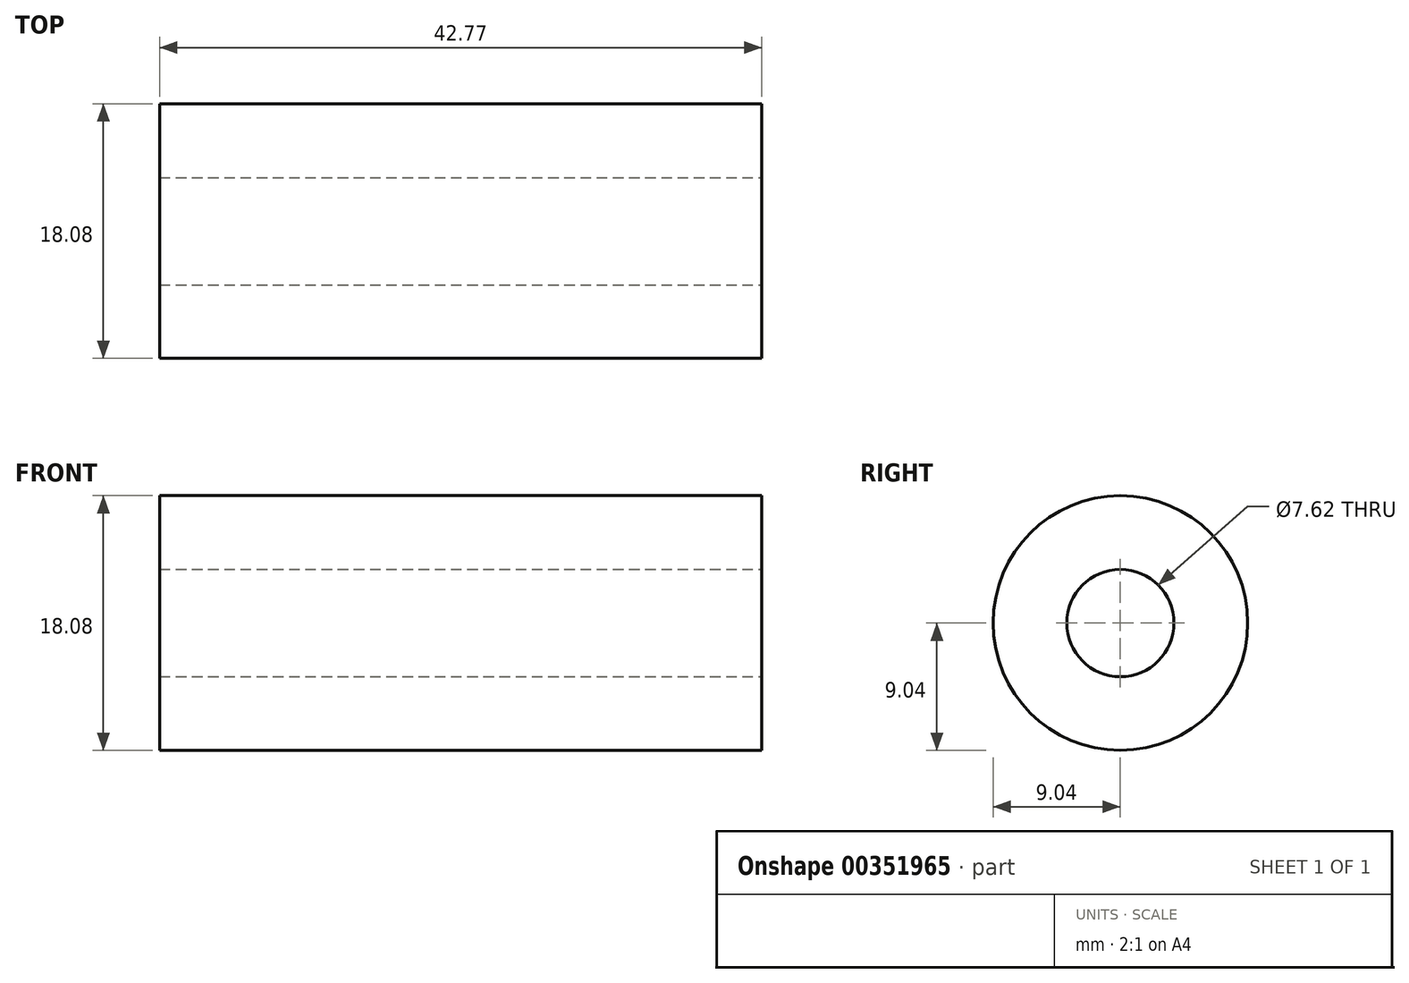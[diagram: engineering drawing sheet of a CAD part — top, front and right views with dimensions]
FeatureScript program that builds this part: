
annotation { "Feature Type Name" : "Feature", "Feature Type Description" : "" }
export const myFeature = defineFeature(function(context is Context, id is Id, definition is map)
    precondition{}
    {
        {
            var Q0;
            Q0=qCreatedBy(makeId("Front.planeOp"),FACE);
            var sketch = newSketch(context, id + "F0", { "sketchPlane" : qUnion([Q0])});
            skLineSegment(sketch, "E0.bottom", {"start": v(0, 0) * mm, "end": v(-42.77, 0) * mm});
            skLineSegment(sketch, "E0.top", {"start": v(0, 9.04) * mm, "end": v(-42.77, 9.04) * mm});
            skLineSegment(sketch, "E0.left", {"start": v(0, 0) * mm, "end": v(0, 9.04) * mm});
            skLineSegment(sketch, "E0.right", {"start": v(-42.77, 0) * mm, "end": v(-42.77, 9.04) * mm});
            skLineSegment(sketch, "E1.bottom", {"start": v(0, 9.04) * mm, "end": v(-25.63, 9.04) * mm});
            skLineSegment(sketch, "E1.top", {"start": v(0, 16.87) * mm, "end": v(-25.63, 16.87) * mm});
            skLineSegment(sketch, "E1.left", {"start": v(0, 9.04) * mm, "end": v(0, 16.87) * mm});
            skLineSegment(sketch, "E1.right", {"start": v(-25.63, 9.04) * mm, "end": v(-25.63, 16.87) * mm});
            skPoint(sketch, "E2", {"position": v(-11.73, 16.87) * mm});
            skLineSegment(sketch, "E3.bottom", {"start": v(-11.73, 16.87) * mm, "end": v(-15.65, 16.87) * mm});
            skLineSegment(sketch, "E3.top", {"start": v(-11.73, 35.94) * mm, "end": v(-15.65, 35.94) * mm});
            skLineSegment(sketch, "E3.left", {"start": v(-11.73, 16.87) * mm, "end": v(-11.73, 35.94) * mm});
            skLineSegment(sketch, "E3.right", {"start": v(-15.65, 16.87) * mm, "end": v(-15.65, 35.94) * mm});
            skSolve(sketch);
        }
        {
            var Q0;
            Q0=makeQuery(id+"F0.imprint","IMPRINT",FACE,{"disambiguationData":[TD([[makeQuery(id+"F0.imprint","IMPRINT",EDGE,{"derivedFrom":sQuery(id+"F0.wireOp",EDGE,"E0.bottom")}),-1.0]])]});
            var Q1;
            Q1=makeQuery(id+"F0.imprint","IMPRINT",FACE,{"disambiguationData":[TD([[makeQuery(id+"F0.imprint","IMPRINT",EDGE,{"derivedFrom":sQuery(id+"F0.wireOp",EDGE,"E1.bottom")}),-1.0]])]});
            var Q2;
            Q2=makeQuery(id+"F0.imprint","IMPRINT",FACE,{"disambiguationData":[TD([[makeQuery(id+"F0.imprint","IMPRINT",EDGE,{"derivedFrom":sQuery(id+"F0.wireOp",EDGE,"E3.bottom")}),-1.0]])]});
            var Q3;
            Q3=sQuery(id+"F0.wireOp",EDGE,"E0.bottom");
            revolve(context, id + "F1", {"entities" : qUnion([Q0, Q1, Q2]), "axis" : qUnion([Q3]), "revolveType" : RevolveType.FULL});
        }
        {
            var Q0;
            Q0=qCreatedBy(makeId("Right.planeOp"),FACE);
            var sketch = newSketch(context, id + "F2", { "sketchPlane" : qUnion([Q0])});
            skCircle(sketch, "E4", {"center": v(0, 0) * mm, "radius": 6.35 * mm});
            skSolve(sketch);
        }
        {
            var Q0;
            Q0=sQuery(id+"F2.wireOp",VERTEX,"E4.center");
            var Q1;
            Q1=makeQuery(id+"F1.opRevolve","SWEPT_BODY",BODY,{"disambiguationData":[OSD([sQuery(id+"F0.wireOp",EDGE,"E0.bottom"),sQuery(id+"F0.wireOp",EDGE,"E0.top"),sQuery(id+"F0.wireOp",EDGE,"E0.left"),sQuery(id+"F0.wireOp",EDGE,"E0.right"),sQuery(id+"F0.wireOp",EDGE,"E1.top"),sQuery(id+"F0.wireOp",EDGE,"E1.left"),sQuery(id+"F0.wireOp",EDGE,"E1.right"),sQuery(id+"F0.wireOp",EDGE,"E3.top"),sQuery(id+"F0.wireOp",EDGE,"E3.left"),sQuery(id+"F0.wireOp",EDGE,"E3.right")])]});
            hole(context, id + "F3", {"style" : HoleStyle.SIMPLE, "endStyle" : HoleEndStyle.THROUGH, "holeDiameter" : 7.62 * mm, "isTappedThrough" : true, "tappedDepth" : 12.7 * mm, "tapClearance" : 3, "locations" : qUnion([Q0]), "scope" : qUnion([Q1])});
        }
    });
